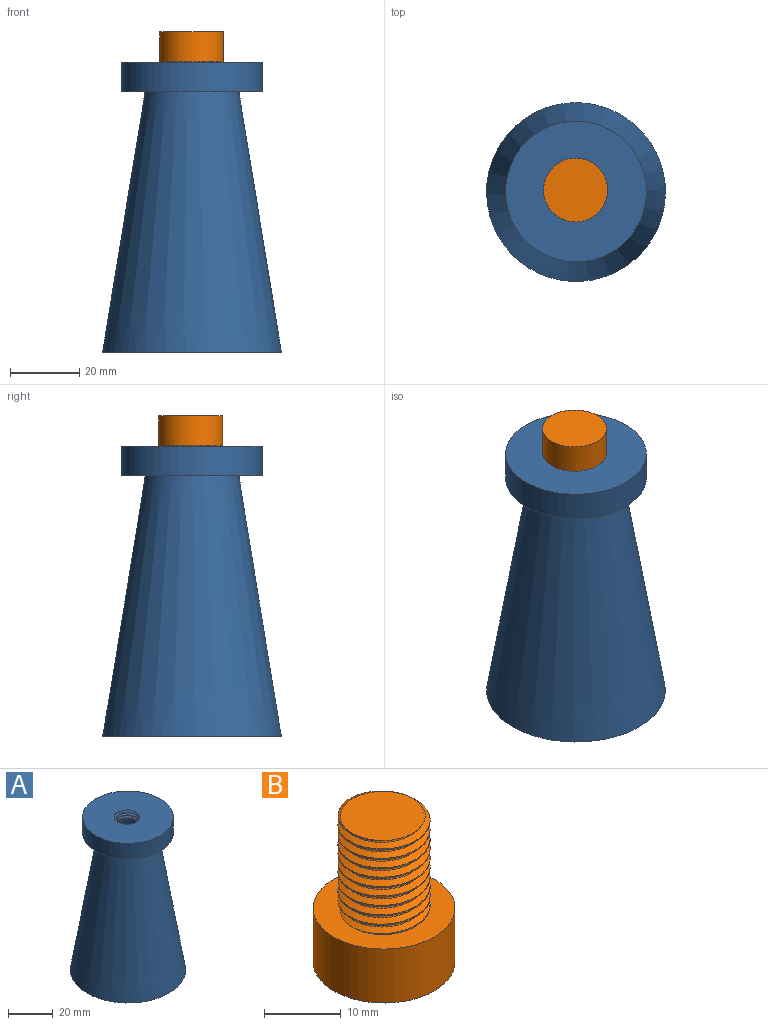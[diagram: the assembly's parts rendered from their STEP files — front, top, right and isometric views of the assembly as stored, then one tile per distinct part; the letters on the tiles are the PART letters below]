
ASSEMBLY  parts=2 mates=1
PART A: 17 faces, bbox 52.2x52.2x85.2 mm
  f0: plane 52.09x52.09mm, normal (0,0,-1), area 875mm2, adj f4,f11,f12,f13,f16
  f1: plane 41.15x41.15mm, normal (0,0,1), area 1201.9mm2, adj f6,f7,f8,f9,f10
  f2: plane 16.24x16.24mm, normal (0,0,-1), area 96.7mm2, adj f3,f7,f8,f9,f10
  f3: cone r=20mm half-angle=9.3deg, axis (0,0,-1), area 6571.9mm2, adj f2,f14,f15
  f4: cone r=25.85mm half-angle=9.3deg, axis (0,0,-1), area 9431.9mm2, adj f0,f5
  f5: plane 40.7x40.7mm, normal (0,0,-1), area 724.2mm2, adj f4,f6
  f6: cylinder r=20.35mm len=40.7mm, axis (0,0,-1), area 1099.6mm2, adj f1,f5
  f7: bspline ~14x12.12mm, area 110.7mm2, adj f1,f2,f9,f10
  f8: bspline ~14x12.12mm, area 111.2mm2, adj f1,f2,f9,f10
  f9: bspline ~14.16x12.26mm, area 27.8mm2, adj f1,f2,f7,f8
  f10: cylinder r=5.25mm len=10.5mm, axis (0,0,-1), area 40.6mm2, adj f1,f2,f7,f8
  f11: bspline ~46.28x40.08mm, area 371.7mm2, adj f0,f13,f14,f15,f16
  f12: bspline ~46.28x40.08mm, area 372.1mm2, adj f0,f13,f14,f15,f16
  f13: bspline ~46.39x40.17mm, area 87.5mm2, adj f0,f11,f12,f14
  f14: plane 17.94x10.59mm, normal (0,0,-1), area 1.1mm2, adj f3,f11,f12,f13
  f15: plane 40.35x40.35mm, normal (0,0,1), area 33.5mm2, adj f3,f11,f12,f16
  f16: cylinder r=19.5mm len=39mm, axis (0,0,1), area 145.6mm2, adj f0,f11,f12,f15
PART B: 8 faces, bbox 18.9x18.9x24.6 mm
  f0: cylinder r=9.25mm len=18.5mm, axis (0,0,-1), area 499.8mm2, adj f1,f2
  f1: plane 18.92x18.92mm, normal (0,0,1), area 172.4mm2, adj f0,f3,f5,f6,f7
  f2: plane 18.5x18.5mm, normal (0,0,-1), area 268.8mm2, adj f0
  f3: cylinder r=6mm len=15mm, axis (0,0,-1), area 101.7mm2, adj f1,f4,f6,f7
  f4: plane 11.55x11.49mm, normal (0,0,1), area 96.4mm2, adj f3,f5,f6,f7
  f5: bspline ~16.13x11.98mm, area 135.7mm2, adj f1,f4,f6,f7
  f6: bspline ~16.22x13.86mm, area 330.1mm2, adj f1,f3,f4,f5
  f7: bspline ~15.97x13.86mm, area 329.8mm2, adj f1,f3,f4,f5
PLACE A rot(axis=(0,0,-1),12.4deg) t=(-27.98,-14.96,-0.32)mm
PLACE B rot(axis=(-0.43,-0.9,0),180deg) t=(-28.11,-14.52,92.24)mm
MATE cylindrical B.f4 <-> A.f3  axis (0,0,-1) through (-27.98,-14.96,68.64)mm
